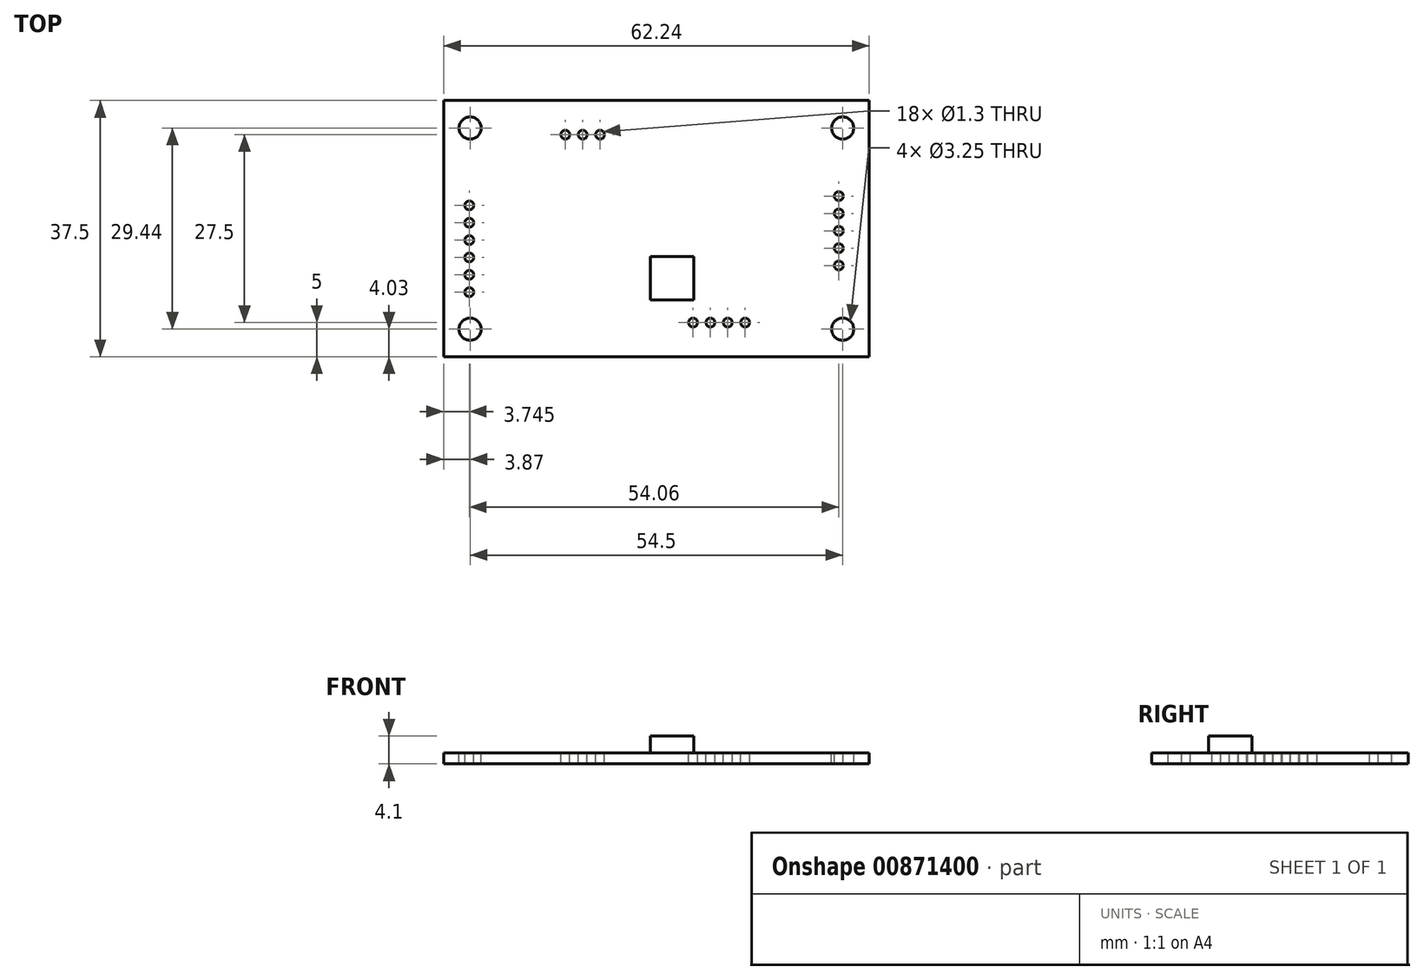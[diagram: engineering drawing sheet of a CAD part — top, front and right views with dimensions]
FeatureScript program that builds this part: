
annotation { "Feature Type Name" : "Feature", "Feature Type Description" : "" }
export const myFeature = defineFeature(function(context is Context, id is Id, definition is map)
    precondition{}
    {
        {
            var Q0;
            Q0=qCreatedBy(makeId("Top.planeOp"),FACE);
            var sketch = newSketch(context, id + "F0", { "sketchPlane" : qUnion([Q0])});
            skLineSegment(sketch, "E0.bottom", {"start": v(-31.12, 18.75) * mm, "end": v(31.12, 18.75) * mm});
            skLineSegment(sketch, "E0.top", {"start": v(-31.12, -18.75) * mm, "end": v(31.12, -18.75) * mm});
            skLineSegment(sketch, "E0.left", {"start": v(-31.12, 18.75) * mm, "end": v(-31.12, -18.75) * mm});
            skLineSegment(sketch, "E0.right", {"start": v(31.12, 18.75) * mm, "end": v(31.12, -18.75) * mm});
            skPoint(sketch, "E0.middle", {"position": v(0, 0) * mm});
            skLineSegment(sketch, "E1", {"start": v(-13.32, 13.75) * mm, "end": v(-10.79, 13.75) * mm, "construction": true});
            skLineSegment(sketch, "E2", {"start": v(-10.79, 13.75) * mm, "end": v(-8.24, 13.75) * mm, "construction": true});
            skPoint(sketch, "E3", {"position": v(-27.38, 3.4) * mm});
            skPoint(sketch, "E4", {"position": v(26.69, -5.4) * mm});
            skLineSegment(sketch, "E5.bottom", {"start": v(-27.25, 14.72) * mm, "end": v(27.25, 14.72) * mm, "construction": true});
            skLineSegment(sketch, "E5.top", {"start": v(-27.25, -14.72) * mm, "end": v(27.25, -14.72) * mm, "construction": true});
            skLineSegment(sketch, "E5.left", {"start": v(-27.25, 14.72) * mm, "end": v(-27.25, -14.72) * mm, "construction": true});
            skLineSegment(sketch, "E5.right", {"start": v(27.25, 14.72) * mm, "end": v(27.25, -14.72) * mm, "construction": true});
            skPoint(sketch, "E6", {"position": v(12.98, -13.75) * mm});
            skPoint(sketch, "E7.0.1.0", {"position": v(-27.38, 0.86) * mm});
            skPoint(sketch, "E7.0.2.0", {"position": v(-27.38, -1.68) * mm});
            skPoint(sketch, "E7.0.3.0", {"position": v(-27.38, -4.22) * mm});
            skPoint(sketch, "E7.0.4.0", {"position": v(-27.38, -6.76) * mm});
            skPoint(sketch, "E7.0.5.0", {"position": v(-27.38, -9.3) * mm});
            skLineSegment(sketch, "E7.direction1", {"start": v(-27.38, 3.4) * mm, "end": v(-24.84, 3.4) * mm, "construction": true});
            skLineSegment(sketch, "E7.direction2", {"start": v(-27.38, 3.4) * mm, "end": v(-27.38, 0.86) * mm, "construction": true});
            skPoint(sketch, "E8.0.1.0", {"position": v(26.68, -2.86) * mm});
            skPoint(sketch, "E8.0.2.0", {"position": v(26.69, -0.32) * mm});
            skPoint(sketch, "E8.0.3.0", {"position": v(26.69, 2.22) * mm});
            skPoint(sketch, "E8.0.4.0", {"position": v(26.69, 4.76) * mm});
            skLineSegment(sketch, "E8.direction1", {"start": v(0, -5.4) * mm, "end": v(26.69, -5.4) * mm, "construction": true});
            skLineSegment(sketch, "E8.direction2", {"start": v(26.68, -5.4) * mm, "end": v(26.68, -2.86) * mm, "construction": true});
            skPoint(sketch, "E9.1.0.0", {"position": v(10.45, -13.75) * mm});
            skPoint(sketch, "E9.2.0.0", {"position": v(7.9, -13.75) * mm});
            skPoint(sketch, "E9.3.0.0", {"position": v(5.37, -13.75) * mm});
            skLineSegment(sketch, "E9.direction1", {"start": v(12.98, -13.75) * mm, "end": v(10.45, -13.75) * mm, "construction": true});
            skLineSegment(sketch, "E10.bottom", {"start": v(-0.87, -4.1) * mm, "end": v(5.48, -4.1) * mm});
            skLineSegment(sketch, "E10.top", {"start": v(-0.87, -10.45) * mm, "end": v(5.48, -10.45) * mm});
            skLineSegment(sketch, "E10.left", {"start": v(-0.87, -4.1) * mm, "end": v(-0.87, -10.45) * mm});
            skLineSegment(sketch, "E10.right", {"start": v(5.48, -4.1) * mm, "end": v(5.48, -10.45) * mm});
            skSolve(sketch);
        }
        {
            var Q0;
            Q0=makeQuery(id+"F0.imprint","IMPRINT",FACE,{"disambiguationData":[TD([[makeQuery(id+"F0.imprint","IMPRINT",EDGE,{"derivedFrom":sQuery(id+"F0.wireOp",EDGE,"E0.bottom")}),-1.0]])]});
            var Q1;
            Q1=makeQuery(id+"F0.imprint","IMPRINT",FACE,{"disambiguationData":[TD([[makeQuery(id+"F0.imprint","IMPRINT",EDGE,{"derivedFrom":sQuery(id+"F0.wireOp",EDGE,"E10.bottom")}),-1.0]])]});
            extrude(context, id + "F1", {"entities" : qUnion([Q0, Q1]), "oppositeDirection" : true, "depth" : 1.6 * mm, "offsetDistance" : 25 * mm});
        }
        {
            var Q0;
            Q0=makeQuery(id+"F0.imprint","IMPRINT",FACE,{"disambiguationData":[TD([[makeQuery(id+"F0.imprint","IMPRINT",EDGE,{"derivedFrom":sQuery(id+"F0.wireOp",EDGE,"E10.bottom")}),-1.0]])]});
            extrude(context, id + "F2", {"entities" : qUnion([Q0]), "operationType" : NewBodyOperationType.ADD, "depth" : 2.5 * mm, "offsetDistance" : 25 * mm});
        }
        {
            var Q0;
            Q0=sQuery(id+"F0.wireOp",VERTEX,"E1.start");
            var Q1;
            Q1=sQuery(id+"F0.wireOp",VERTEX,"E1.end");
            var Q2;
            Q2=sQuery(id+"F0.wireOp",VERTEX,"E2.end");
            var Q3;
            Q3=sQuery(id+"F0.wireOp",VERTEX,"E3");
            var Q4;
            Q4=sQuery(id+"F0.wireOp",VERTEX,"E7.0.1.0");
            var Q5;
            Q5=sQuery(id+"F0.wireOp",VERTEX,"E7.0.2.0");
            var Q6;
            Q6=sQuery(id+"F0.wireOp",VERTEX,"E7.0.3.0");
            var Q7;
            Q7=sQuery(id+"F0.wireOp",VERTEX,"E7.0.4.0");
            var Q8;
            Q8=sQuery(id+"F0.wireOp",VERTEX,"E7.0.5.0");
            var Q9;
            Q9=sQuery(id+"F0.wireOp",VERTEX,"E9.3.0.0");
            var Q10;
            Q10=sQuery(id+"F0.wireOp",VERTEX,"E9.2.0.0");
            var Q11;
            Q11=sQuery(id+"F0.wireOp",VERTEX,"E9.1.0.0");
            var Q12;
            Q12=sQuery(id+"F0.wireOp",VERTEX,"E6");
            var Q13;
            Q13=sQuery(id+"F0.wireOp",VERTEX,"E4");
            var Q14;
            Q14=sQuery(id+"F0.wireOp",VERTEX,"E8.0.1.0");
            var Q15;
            Q15=sQuery(id+"F0.wireOp",VERTEX,"E8.0.2.0");
            var Q16;
            Q16=sQuery(id+"F0.wireOp",VERTEX,"E8.0.3.0");
            var Q17;
            Q17=sQuery(id+"F0.wireOp",VERTEX,"E8.0.4.0");
            var Q18;
            Q18=makeQuery(id+"F1.opExtrude","SWEPT_BODY",BODY,{"disambiguationData":[OSD([sQuery(id+"F0.wireOp",EDGE,"E0.bottom"),sQuery(id+"F0.wireOp",EDGE,"E0.top"),sQuery(id+"F0.wireOp",EDGE,"E0.left"),sQuery(id+"F0.wireOp",EDGE,"E0.right")])]});
            hole(context, id + "F3", {"style" : HoleStyle.SIMPLE, "endStyle" : HoleEndStyle.THROUGH, "holeDiameter" : 1.3 * mm, "majorDiameter" : 5 * mm, "isTappedThrough" : true, "tappedDepth" : 12 * mm, "tapClearance" : 3, "startFromSketch" : true, "locations" : qUnion([Q0, Q1, Q2, Q3, Q4, Q5, Q6, Q7, Q8, Q9, Q10, Q11, Q12, Q13, Q14, Q15, Q16, Q17]), "scope" : qUnion([Q18])});
        }
        {
            var Q0;
            Q0=sQuery(id+"F0.wireOp",VERTEX,"E5.bottom.start");
            var Q1;
            Q1=sQuery(id+"F0.wireOp",VERTEX,"E5.top.start");
            var Q2;
            Q2=sQuery(id+"F0.wireOp",VERTEX,"E5.top.end");
            var Q3;
            Q3=sQuery(id+"F0.wireOp",VERTEX,"E5.bottom.end");
            var Q4;
            Q4=makeQuery(id+"F1.opExtrude","SWEPT_BODY",BODY,{"disambiguationData":[OSD([sQuery(id+"F0.wireOp",EDGE,"E0.bottom"),sQuery(id+"F0.wireOp",EDGE,"E0.top"),sQuery(id+"F0.wireOp",EDGE,"E0.left"),sQuery(id+"F0.wireOp",EDGE,"E0.right")])]});
            hole(context, id + "F4", {"style" : HoleStyle.SIMPLE, "endStyle" : HoleEndStyle.THROUGH, "holeDiameter" : 3.25 * mm, "majorDiameter" : 5 * mm, "isTappedThrough" : true, "tappedDepth" : 12 * mm, "tapClearance" : 3, "startFromSketch" : true, "locations" : qUnion([Q0, Q1, Q2, Q3]), "scope" : qUnion([Q4])});
        }
    });
